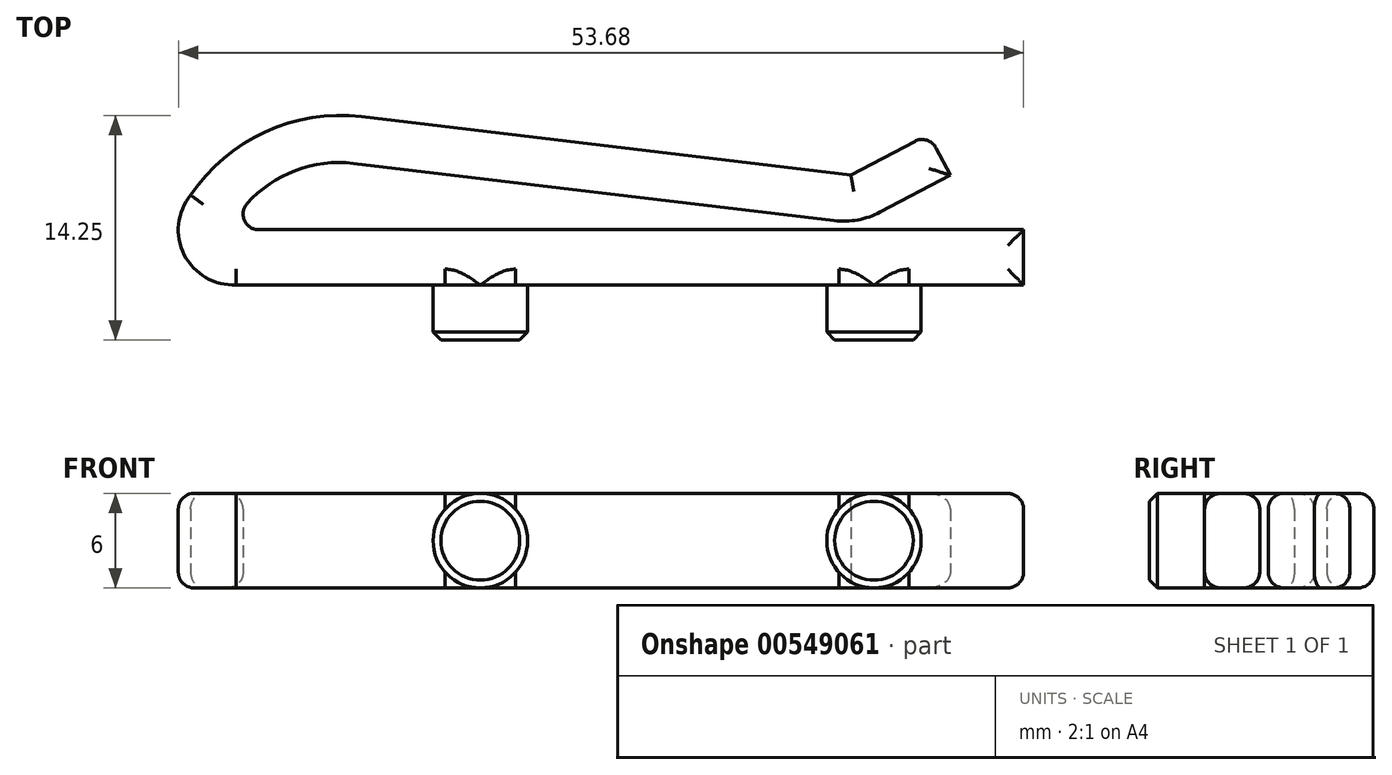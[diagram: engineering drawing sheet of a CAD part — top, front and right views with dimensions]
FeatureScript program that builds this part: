
annotation { "Feature Type Name" : "Feature", "Feature Type Description" : "" }
export const myFeature = defineFeature(function(context is Context, id is Id, definition is map)
    precondition{}
    {
        {
            var Q0;
            Q0=qCreatedBy(makeId("Top.planeOp"),FACE);
            var sketch = newSketch(context, id + "F0", { "sketchPlane" : qUnion([Q0])});
            skLineSegment(sketch, "E0.bottom", {"start": v(1.43, 0) * mm, "end": v(50, 0) * mm});
            skLineSegment(sketch, "E0.top", {"start": v(0, -3.5) * mm, "end": v(50, -3.5) * mm});
            skLineSegment(sketch, "E0.right", {"start": v(50, 0) * mm, "end": v(50, -3.5) * mm});
            skArc(sketch, "E1", {"start": v(7.96, 7.17) * mm, "mid": v(1.83, 6.21) * mm, "end": v(-2.9, 2.2) * mm});
            skArc(sketch, "E2", {"start": v(7.45, 4.21) * mm, "mid": v(3.76, 3.76) * mm, "end": v(0.69, 1.66) * mm});
            skPoint(sketch, "E0.left.start.orphan", {"position": v(0, 0) * mm});
            skArc(sketch, "E3.trimOffspring", {"start": v(-2.9, 2.2) * mm, "mid": v(-3.3, -1.6) * mm, "end": v(0, -3.5) * mm});
            skArc(sketch, "E4", {"start": v(0.69, 1.66) * mm, "mid": v(0.52, 0.59) * mm, "end": v(1.43, 0) * mm});
            skLineSegment(sketch, "E5", {"start": v(7.45, 4.21) * mm, "end": v(39.52, 0.4) * mm});
            skLineSegment(sketch, "E6", {"start": v(7.96, 7.17) * mm, "end": v(39.03, 3.47) * mm});
            skLineSegment(sketch, "E7", {"start": v(39.03, 3.47) * mm, "end": v(43.97, 6.08) * mm});
            skLineSegment(sketch, "E8", {"start": v(43.97, 6.08) * mm, "end": v(45.35, 3.47) * mm});
            skLineSegment(sketch, "E9", {"start": v(45.35, 3.47) * mm, "end": v(39.52, 0.4) * mm});
            skSolve(sketch);
        }
        {
            var Q0;
            Q0=qSketchRegion(id+"F0",true);
            extrude(context, id + "F1", {"entities" : qUnion([Q0]), "depth" : 6 * mm, "offsetDistance" : 25 * mm});
        }
        {
            var Q0;
            Q0=makeQuery(id+"F1.opExtrude","SWEPT_EDGE",EDGE,{"disambiguationData":[OSD([sQuery(id+"F0.wireOp",EDGE,"E5"),sQuery(id+"F0.wireOp",EDGE,"E9")])]});
            fillet(context, id + "F2", {"entities" : qUnion([Q0]), "radius" : 5 * mm, "tangentPropagation" : true, "allowEdgeOverflow" : false});
        }
        {
            var Q0;
            Q0=makeQuery(id+"F1.opExtrude","SWEPT_EDGE",EDGE,{"disambiguationData":[OSD([sQuery(id+"F0.wireOp",EDGE,"E7"),sQuery(id+"F0.wireOp",EDGE,"E8")])]});
            fillet(context, id + "F3", {"entities" : qUnion([Q0]), "radius" : 1 * mm, "tangentPropagation" : true, "allowEdgeOverflow" : false});
        }
        {
            var Q0;
            Q0=makeQuery(id+"F1.opExtrude","SWEPT_FACE",FACE,{"disambiguationData":[OSD([sQuery(id+"F0.wireOp",EDGE,"E0.top")])]});
            var sketch = newSketch(context, id + "F4", { "sketchPlane" : qUnion([Q0])});
            skCircle(sketch, "E10", {"center": v(15.5, 3) * mm, "radius": 3 * mm});
            skPoint(sketch, "E10.centerSnap0", {"position": v(0, 3) * mm});
            skCircle(sketch, "E11", {"center": v(40.5, 3) * mm, "radius": 3 * mm});
            skLineSegment(sketch, "E12", {"start": v(0, 3) * mm, "end": v(15.5, 3) * mm, "construction": true});
            skLineSegment(sketch, "E13", {"start": v(40.5, 3) * mm, "end": v(15.5, 3) * mm, "construction": true});
            skSolve(sketch);
        }
        {
            var Q0;
            Q0 = qSketchRegion(id + "F4", true);
            extrude(context, id + "F5", {"entities" : qUnion([Q0]), "operationType" : NewBodyOperationType.ADD, "depth" : 3.5 * mm, "offsetDistance" : 25 * mm});
        }
        {
            var Q0;
            Q0=makeQuery(id+"F5.opExtrude","CAP_EDGE",EDGE,{"disambiguationData":[OSD([sQuery(id+"F4.wireOp",EDGE,"E10")])],"isStart":false});
            var Q1;
            Q1=makeQuery(id+"F5.opExtrude","CAP_EDGE",EDGE,{"disambiguationData":[OSD([sQuery(id+"F4.wireOp",EDGE,"E11")])],"isStart":false});
            chamfer(context, id + "F6", {"entities" : qUnion([Q0, Q1]), "width" : 0.5 * mm, "tangentPropagation" : true});
        }
        {
            var Q0;
            Q0=makeQuery(id+"F1.opExtrude","CAP_EDGE",EDGE,{"disambiguationData":[OSD([sQuery(id+"F0.wireOp",EDGE,"E6")])],"isStart":false});
            var Q1;
            Q1=makeQuery(id+"F1.opExtrude","CAP_FACE",FACE,{"disambiguationData":[OSD([sQuery(id+"F0.wireOp",EDGE,"E0.bottom"),sQuery(id+"F0.wireOp",EDGE,"E0.top"),sQuery(id+"F0.wireOp",EDGE,"E0.right"),sQuery(id+"F0.wireOp",EDGE,"E1"),sQuery(id+"F0.wireOp",EDGE,"E2"),sQuery(id+"F0.wireOp",EDGE,"E3.trimOffspring"),sQuery(id+"F0.wireOp",EDGE,"E4"),sQuery(id+"F0.wireOp",EDGE,"E5"),sQuery(id+"F0.wireOp",EDGE,"E6"),sQuery(id+"F0.wireOp",EDGE,"E7"),sQuery(id+"F0.wireOp",EDGE,"E8"),sQuery(id+"F0.wireOp",EDGE,"E9")])],"isStart":false});
            var Q2;
            Q2=makeQuery(id+"F1.opExtrude","CAP_FACE",FACE,{"disambiguationData":[OSD([sQuery(id+"F0.wireOp",EDGE,"E0.bottom"),sQuery(id+"F0.wireOp",EDGE,"E0.top"),sQuery(id+"F0.wireOp",EDGE,"E0.right"),sQuery(id+"F0.wireOp",EDGE,"E1"),sQuery(id+"F0.wireOp",EDGE,"E2"),sQuery(id+"F0.wireOp",EDGE,"E3.trimOffspring"),sQuery(id+"F0.wireOp",EDGE,"E4"),sQuery(id+"F0.wireOp",EDGE,"E5"),sQuery(id+"F0.wireOp",EDGE,"E6"),sQuery(id+"F0.wireOp",EDGE,"E7"),sQuery(id+"F0.wireOp",EDGE,"E8"),sQuery(id+"F0.wireOp",EDGE,"E9")])],"isStart":true});
            fillet(context, id + "F7", {"entities" : qUnion([Q0, Q1, Q2]), "radius" : 1 * mm, "tangentPropagation" : true, "allowEdgeOverflow" : false});
        }
    });
